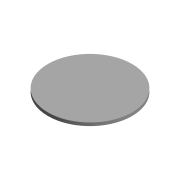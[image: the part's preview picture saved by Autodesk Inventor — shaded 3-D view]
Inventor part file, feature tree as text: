
AUTODESK INVENTOR PART (.ipt)
format: ipt  version: 2014 (Build 180170000, 170)  size: 68,096 bytes
history: native  units: mm
features: sketch x1, plane x1, extrude x1, reference x1
ambient origin geometry x8: Origin, YZ Plane, XZ Plane, XY Plane, X Axis, Y Axis, Z Axis, Center Point
bodies: Volumenkörper1 (feature_tree)
feature tree (4):
  sketch  "Skizze1"  dims[d0=0.5mm d1=1.0mm d2=0.0mm]
  plane  "Arbeitsebene1"
  extrude  "Extrusion1"  Depth=1.0mm TaperAngle=0.0deg
  reference  "Referenz1"
